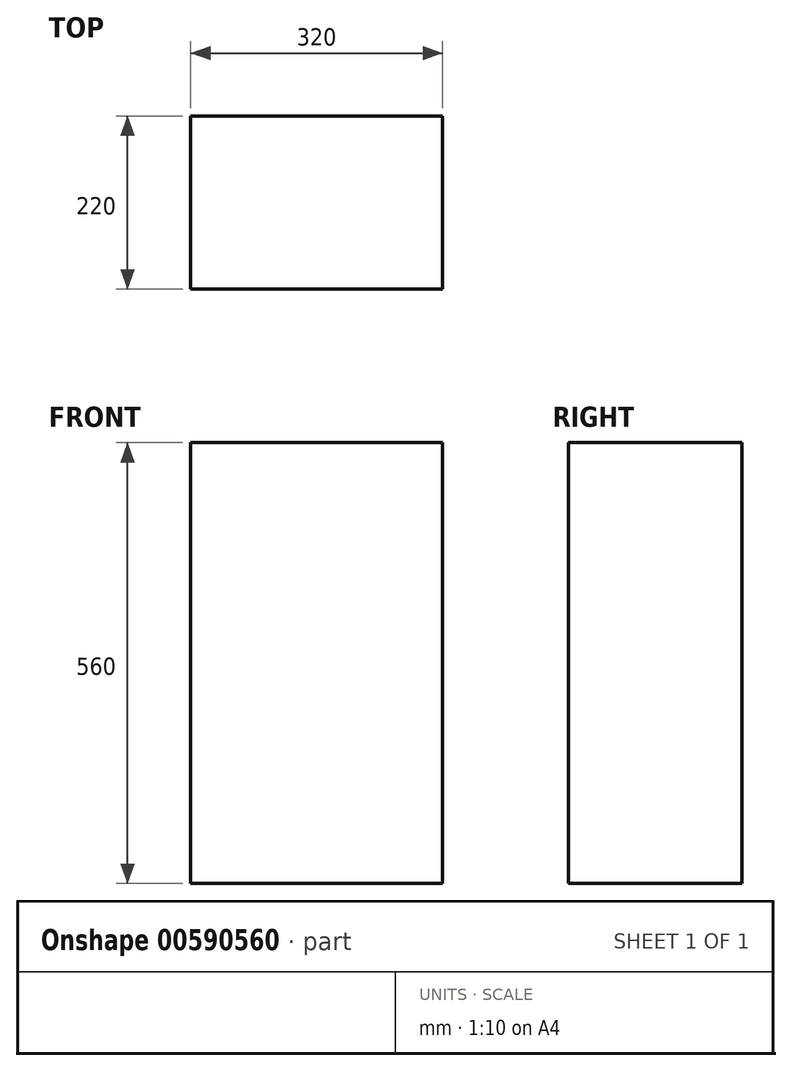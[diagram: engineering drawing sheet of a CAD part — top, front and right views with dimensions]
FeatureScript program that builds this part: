
annotation { "Feature Type Name" : "Feature", "Feature Type Description" : "" }
export const myFeature = defineFeature(function(context is Context, id is Id, definition is map)
    precondition{}
    {
        {
            var Q0;
            Q0=qCreatedBy(makeId("Front.planeOp"),FACE);
            var sketch = newSketch(context, id + "F0", { "sketchPlane" : qUnion([Q0])});
            skLineSegment(sketch, "E0.bottom", {"start": v(-149.38, 338.22) * mm, "end": v(170.62, 338.22) * mm});
            skLineSegment(sketch, "E0.top", {"start": v(-149.38, -221.78) * mm, "end": v(170.62, -221.78) * mm});
            skLineSegment(sketch, "E0.left", {"start": v(-149.38, 338.22) * mm, "end": v(-149.38, -221.78) * mm});
            skLineSegment(sketch, "E0.right", {"start": v(170.62, 338.22) * mm, "end": v(170.62, -221.78) * mm});
            skSolve(sketch);
        }
        {
            var Q0;
            Q0=makeQuery(id+"F0.imprint","IMPRINT",FACE,{"disambiguationData":[TD([[makeQuery(id+"F0.imprint","IMPRINT",EDGE,{"derivedFrom":sQuery(id+"F0.wireOp",EDGE,"E0.bottom")}),-1.0]])]});
            extrude(context, id + "F1", {"entities" : qUnion([Q0]), "depth" : 220 * mm, "offsetDistance" : 25.4 * mm});
        }
        {
            var Q0;
            Q0=makeQuery(id+"F1.opExtrude","SWEPT_FACE",FACE,{"disambiguationData":[OSD([sQuery(id+"F0.wireOp",EDGE,"E0.bottom")])]});
            var sketch = newSketch(context, id + "F2", { "sketchPlane" : qUnion([Q0])});
            skLineSegment(sketch, "E1.bottom", {"start": v(-139.38, -10) * mm, "end": v(160.62, -10) * mm});
            skLineSegment(sketch, "E1.top", {"start": v(-139.38, -210) * mm, "end": v(160.62, -210) * mm});
            skLineSegment(sketch, "E1.left", {"start": v(-139.38, -10) * mm, "end": v(-139.38, -210) * mm});
            skLineSegment(sketch, "E1.right", {"start": v(160.62, -10) * mm, "end": v(160.62, -210) * mm});
            skSolve(sketch);
        }
        {
            var Q0;
            Q0=makeQuery(id+"F2.imprint","IMPRINT",FACE,{"disambiguationData":[TD([[makeQuery(id+"F2.imprint","IMPRINT",EDGE,{"derivedFrom":sQuery(id+"F2.wireOp",EDGE,"E1.bottom")}),-1.0]])]});
            extrude(context, id + "F3", {"entities" : qUnion([Q0]), "operationType" : NewBodyOperationType.ADD, "depth" : -20 * mm, "offsetDistance" : 25.4 * mm});
        }
    });
